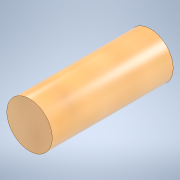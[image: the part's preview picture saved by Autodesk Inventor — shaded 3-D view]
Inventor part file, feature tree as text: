
AUTODESK INVENTOR PART (.ipt)
format: ipt  version: 2021 (Build 250183000, 183)  size: 104,448 bytes
history: native  units: mm
features: other x1, extrude x1, sketch x1
ambient origin geometry x8: Origin, YZ Plane, XZ Plane, XY Plane, X Axis, Y Axis, Z Axis, Center Point
bodies: Body1 (feature_tree)
feature tree (3):
  other  "Sólido1"
  extrude  "Extrusão1"  Depth=8.0mm TaperAngle=0.0deg
  sketch  "Esboço1"  dims[d0=3.0mm d1=8.0mm d2=0.0mm]
